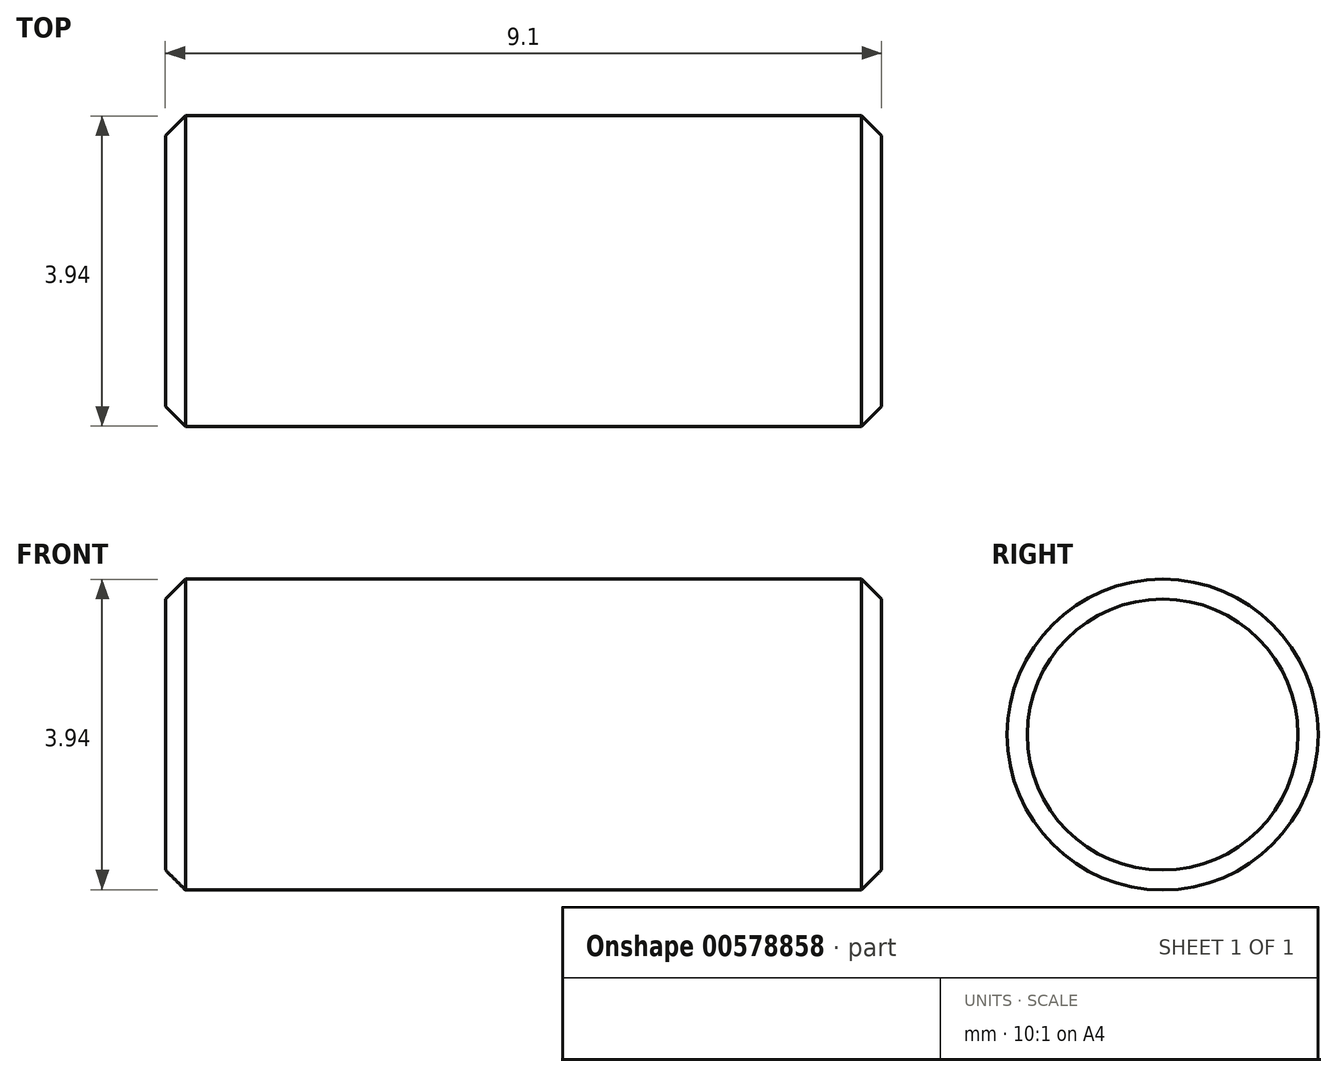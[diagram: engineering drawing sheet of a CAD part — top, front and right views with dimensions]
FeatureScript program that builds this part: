
annotation { "Feature Type Name" : "Feature", "Feature Type Description" : "" }
export const myFeature = defineFeature(function(context is Context, id is Id, definition is map)
    precondition{}
    {
        {
            var Q0;
            Q0=qCreatedBy(makeId("Right.planeOp"),FACE);
            var sketch = newSketch(context, id + "F0", { "sketchPlane" : qUnion([Q0])});
            skCircle(sketch, "E0", {"center": v(0, 0) * mm, "radius": 1.97 * mm});
            skSolve(sketch);
        }
        {
            var Q0;
            Q0=makeQuery(id+"F0.imprint","IMPRINT",FACE,{"disambiguationData":[TD([[makeQuery(id+"F0.imprint","IMPRINT",EDGE,{"derivedFrom":sQuery(id+"F0.wireOp",EDGE,"E0")}),1.0]])]});
            extrude(context, id + "F1", {"entities" : qUnion([Q0]), "endBound" : BoundingType.SYMMETRIC, "depth" : 9.1 * mm});
        }
        {
            var Q0;
            Q0=makeQuery(id+"F1.opExtrude","CAP_EDGE",EDGE,{"disambiguationData":[OSD([sQuery(id+"F0.wireOp",EDGE,"E0")])],"isStart":true});
            var Q1;
            Q1=makeQuery(id+"F1.opExtrude","CAP_EDGE",EDGE,{"disambiguationData":[OSD([sQuery(id+"F0.wireOp",EDGE,"E0")])],"isStart":false});
            chamfer(context, id + "F2", {"entities" : qUnion([Q0, Q1]), "width" : 0.25 * mm, "tangentPropagation" : true});
        }
    });
